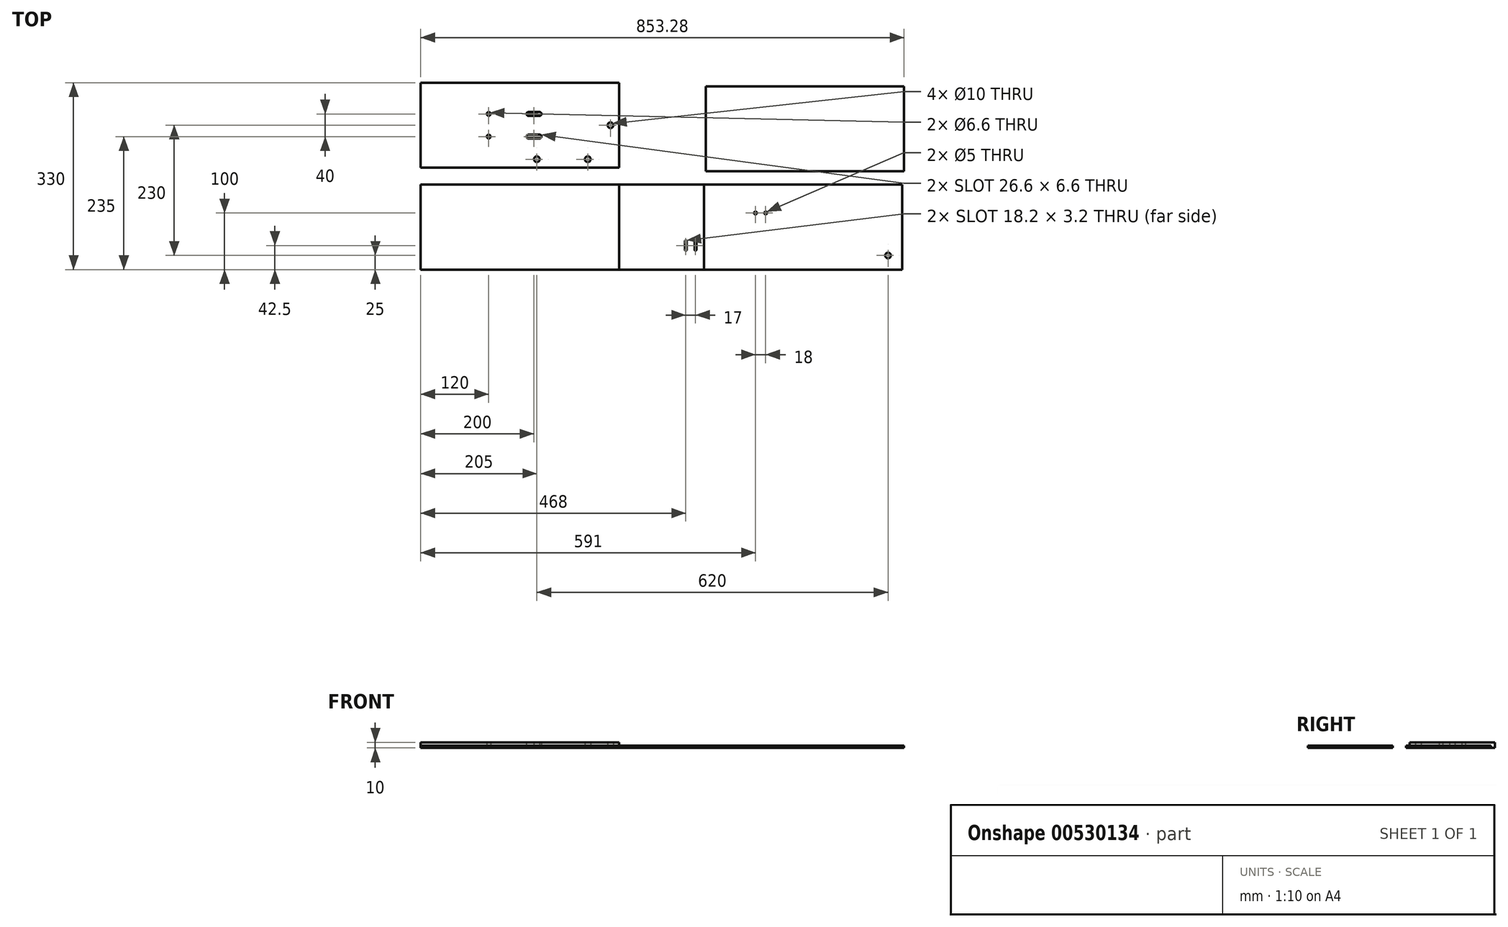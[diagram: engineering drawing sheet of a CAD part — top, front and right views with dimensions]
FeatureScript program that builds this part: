
annotation { "Feature Type Name" : "Feature", "Feature Type Description" : "" }
export const myFeature = defineFeature(function(context is Context, id is Id, definition is map)
    precondition{}
    {
        {
            var Q0;
            Q0=qCreatedBy(makeId("Top.planeOp"),FACE);
            var sketch = newSketch(context, id + "F0", { "sketchPlane" : qUnion([Q0])});
            skLineSegment(sketch, "E0.bottom", {"start": v(75, 75) * mm, "end": v(-75, 75) * mm});
            skLineSegment(sketch, "E0.top", {"start": v(75, -75) * mm, "end": v(-75, -75) * mm});
            skLineSegment(sketch, "E0.left", {"start": v(75, 75) * mm, "end": v(75, -75) * mm});
            skLineSegment(sketch, "E0.right", {"start": v(-75, 75) * mm, "end": v(-75, -75) * mm});
            skPoint(sketch, "E0.middle", {"position": v(0, 0) * mm});
            skLineSegment(sketch, "E1.bottom", {"start": v(75, -75) * mm, "end": v(425, -75) * mm});
            skLineSegment(sketch, "E1.top", {"start": v(75, 75) * mm, "end": v(425, 75) * mm});
            skLineSegment(sketch, "E1.left", {"start": v(75, -75) * mm, "end": v(75, 75) * mm});
            skLineSegment(sketch, "E1.right", {"start": v(425, -75) * mm, "end": v(425, 75) * mm});
            skLineSegment(sketch, "E2.bottom", {"start": v(-75, -75) * mm, "end": v(-425, -75) * mm});
            skLineSegment(sketch, "E2.top", {"start": v(-75, 75) * mm, "end": v(-425, 75) * mm});
            skLineSegment(sketch, "E2.left", {"start": v(-75, -75) * mm, "end": v(-75, 75) * mm});
            skLineSegment(sketch, "E2.right", {"start": v(-425, -75) * mm, "end": v(-425, 75) * mm});
            skLineSegment(sketch, "E3", {"start": v(60, -40) * mm, "end": v(60, -25) * mm, "construction": true});
            skLineSegment(sketch, "E4", {"start": v(43, -40) * mm, "end": v(43, -25) * mm, "construction": true});
            skArc(sketch, "E5.0.startCap", {"start": v(61.6, -40) * mm, "mid": v(60, -41.6) * mm, "end": v(58.4, -40) * mm});
            skArc(sketch, "E5.0.endCap", {"start": v(58.4, -25) * mm, "mid": v(60, -23.4) * mm, "end": v(61.6, -25) * mm});
            skLineSegment(sketch, "E5.0.left", {"start": v(58.4, -40) * mm, "end": v(58.4, -25) * mm});
            skLineSegment(sketch, "E5.0.right", {"start": v(61.6, -40) * mm, "end": v(61.6, -25) * mm});
            skArc(sketch, "E5.1.startCap", {"start": v(44.6, -40) * mm, "mid": v(43, -41.6) * mm, "end": v(41.4, -40) * mm});
            skArc(sketch, "E5.1.endCap", {"start": v(41.4, -25) * mm, "mid": v(43, -23.4) * mm, "end": v(44.6, -25) * mm});
            skLineSegment(sketch, "E5.1.left", {"start": v(41.4, -40) * mm, "end": v(41.4, -25) * mm});
            skLineSegment(sketch, "E5.1.right", {"start": v(44.6, -40) * mm, "end": v(44.6, -25) * mm});
            skCircle(sketch, "E6", {"center": v(400, -50) * mm, "radius": 5 * mm});
            skCircle(sketch, "E7", {"center": v(166, 25) * mm, "radius": 2.5 * mm});
            skCircle(sketch, "E8", {"center": v(184, 25) * mm, "radius": 2.5 * mm});
            skLineSegment(sketch, "E9", {"start": v(175, 32.74) * mm, "end": v(175, 49.93) * mm, "construction": true});
            skLineSegment(sketch, "E10.bottom", {"start": v(400, -50) * mm, "end": v(425, -50) * mm, "construction": true});
            skLineSegment(sketch, "E10.top", {"start": v(400, -75) * mm, "end": v(425, -75) * mm, "construction": true});
            skLineSegment(sketch, "E10.left", {"start": v(400, -50) * mm, "end": v(400, -75) * mm, "construction": true});
            skLineSegment(sketch, "E10.right", {"start": v(425, -50) * mm, "end": v(425, -75) * mm, "construction": true});
            skSolve(sketch);
        }
        {
            var Q0;
            Q0=makeQuery(id+"F0.imprint","IMPRINT",FACE,{"disambiguationData":[TD([[makeQuery(id+"F0.imprint","IMPRINT",EDGE,{"derivedFrom":sQuery(id+"F0.wireOp",EDGE,"E2.bottom")}),-1.0]])]});
            var Q1;
            Q1=makeQuery(id+"F0.imprint","IMPRINT",FACE,{"disambiguationData":[TD([[makeQuery(id+"F0.imprint","IMPRINT",EDGE,{"derivedFrom":sQuery(id+"F0.wireOp",EDGE,"E1.bottom")}),1.0]])]});
            extrude(context, id + "F1", {"entities" : qUnion([Q0, Q1]), "depth" : 4 * mm, "offsetDistance" : 25 * mm});
        }
        {
            var Q0;
            Q0=makeQuery(id+"F0.imprint","IMPRINT",FACE,{"disambiguationData":[TD([[makeQuery(id+"F0.imprint","IMPRINT",EDGE,{"derivedFrom":sQuery(id+"F0.wireOp",EDGE,"E0.bottom")}),1.0]])]});
            extrude(context, id + "F2", {"entities" : qUnion([Q0]), "depth" : 4.1 * mm, "offsetDistance" : 25 * mm});
        }
        {
            var Q0;
            Q0=qCreatedBy(makeId("Top.planeOp"),FACE);
            var sketch = newSketch(context, id + "F3", { "sketchPlane" : qUnion([Q0])});
            skLineSegment(sketch, "E11.bottom", {"start": v(-425, 105) * mm, "end": v(-75, 105) * mm});
            skLineSegment(sketch, "E11.top", {"start": v(-425, 255) * mm, "end": v(-75, 255) * mm});
            skLineSegment(sketch, "E11.left", {"start": v(-425, 105) * mm, "end": v(-425, 255) * mm});
            skLineSegment(sketch, "E11.right", {"start": v(-75, 105) * mm, "end": v(-75, 255) * mm});
            skCircle(sketch, "E12", {"center": v(-90, 180) * mm, "radius": 5 * mm});
            skLineSegment(sketch, "E13", {"start": v(-235, 200) * mm, "end": v(-215, 200) * mm, "construction": true});
            skLineSegment(sketch, "E14", {"start": v(-235, 160) * mm, "end": v(-215, 160) * mm, "construction": true});
            skLineSegment(sketch, "E15", {"start": v(-75, 180) * mm, "end": v(-425, 180) * mm, "construction": true});
            skCircle(sketch, "E16", {"center": v(-130, 120) * mm, "radius": 5 * mm});
            skCircle(sketch, "E17", {"center": v(-220, 120) * mm, "radius": 5 * mm});
            skCircle(sketch, "E18", {"center": v(-305, 200) * mm, "radius": 3.3 * mm});
            skCircle(sketch, "E19", {"center": v(-305, 160) * mm, "radius": 3.3 * mm});
            skLineSegment(sketch, "E20", {"start": v(-175, 149.72) * mm, "end": v(-175, 111.23) * mm, "construction": true});
            skLineSegment(sketch, "E21", {"start": v(-225, 145.9) * mm, "end": v(-225, 211.84) * mm, "construction": true});
            skPoint(sketch, "E21.startSnap0", {"position": v(-225, 160) * mm});
            skArc(sketch, "E22.0.startCap", {"start": v(-215, 203.3) * mm, "mid": v(-211.7, 200) * mm, "end": v(-215, 196.7) * mm});
            skArc(sketch, "E22.0.endCap", {"start": v(-235, 196.7) * mm, "mid": v(-238.3, 200) * mm, "end": v(-235, 203.3) * mm});
            skLineSegment(sketch, "E22.0.left", {"start": v(-235, 196.7) * mm, "end": v(-215, 196.7) * mm});
            skLineSegment(sketch, "E22.0.right", {"start": v(-235, 203.3) * mm, "end": v(-215, 203.3) * mm});
            skArc(sketch, "E22.1.startCap", {"start": v(-215, 163.3) * mm, "mid": v(-211.7, 160) * mm, "end": v(-215, 156.7) * mm});
            skArc(sketch, "E22.1.endCap", {"start": v(-235, 156.7) * mm, "mid": v(-238.3, 160) * mm, "end": v(-235, 163.3) * mm});
            skLineSegment(sketch, "E22.1.left", {"start": v(-235, 156.7) * mm, "end": v(-215, 156.7) * mm});
            skLineSegment(sketch, "E22.1.right", {"start": v(-235, 163.3) * mm, "end": v(-215, 163.3) * mm});
            skSolve(sketch);
        }
        {
            var Q0;
            Q0=makeQuery(id+"F3.imprint","IMPRINT",FACE,{"disambiguationData":[TD([[makeQuery(id+"F3.imprint","IMPRINT",EDGE,{"derivedFrom":sQuery(id+"F3.wireOp",EDGE,"E11.bottom")}),1.0]])]});
            extrude(context, id + "F4", {"entities" : qUnion([Q0]), "depth" : 10 * mm, "offsetDistance" : 25 * mm});
        }
        {
            var Q0;
            Q0=qCreatedBy(makeId("Top.planeOp"),FACE);
            var sketch = newSketch(context, id + "F5", { "sketchPlane" : qUnion([Q0])});
            skLineSegment(sketch, "E23.bottom", {"start": v(78.28, 98.53) * mm, "end": v(428.28, 98.53) * mm});
            skLineSegment(sketch, "E23.top", {"start": v(78.28, 248.53) * mm, "end": v(428.28, 248.53) * mm});
            skLineSegment(sketch, "E23.left", {"start": v(78.28, 98.53) * mm, "end": v(78.28, 248.53) * mm});
            skLineSegment(sketch, "E23.right", {"start": v(428.28, 98.53) * mm, "end": v(428.28, 248.53) * mm});
            skSolve(sketch);
        }
        {
            var Q0;
            Q0=makeQuery(id+"F5.imprint","IMPRINT",FACE,{"disambiguationData":[TD([[makeQuery(id+"F5.imprint","IMPRINT",EDGE,{"derivedFrom":sQuery(id+"F5.wireOp",EDGE,"E23.bottom")}),1.0]])]});
            extrude(context, id + "F6", {"entities" : qUnion([Q0]), "depth" : 4 * mm, "offsetDistance" : 25 * mm});
        }
    });
